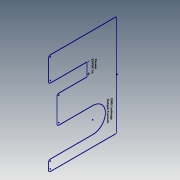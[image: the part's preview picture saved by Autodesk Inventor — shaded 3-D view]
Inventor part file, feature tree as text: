
AUTODESK INVENTOR PART (.ipt)
format: ipt  version: 2020.5 (Build 245400000, 400)  size: 134,144 bytes
history: native  units: mm
features: sketch x1
ambient origin geometry x8: Origin, YZ Plane, XZ Plane, XY Plane, X Axis, Y Axis, Z Axis, Center Point
feature tree (1):
  sketch  "Sketch32"  dims[d13=18.0mm d14=60.0mm d708=18.6mm d709=2.7mm d710=2.7mm d711=21.1mm d712=17.761013mm d713=4.351086mm d714=16.511013mm d715=8.051086mm d716=2.1mm d717=2.1mm d718=8.9mm d719=13.1mm d720=2.6mm d721=3.3mm d722=1.8mm d723=0.6mm d724=23.909893mm d725=26.009893mm d726=20.194718mm d727=23.294718mm d728=26.905472mm d729=27.908194mm d730=16.158484mm d731=26.020802mm]
